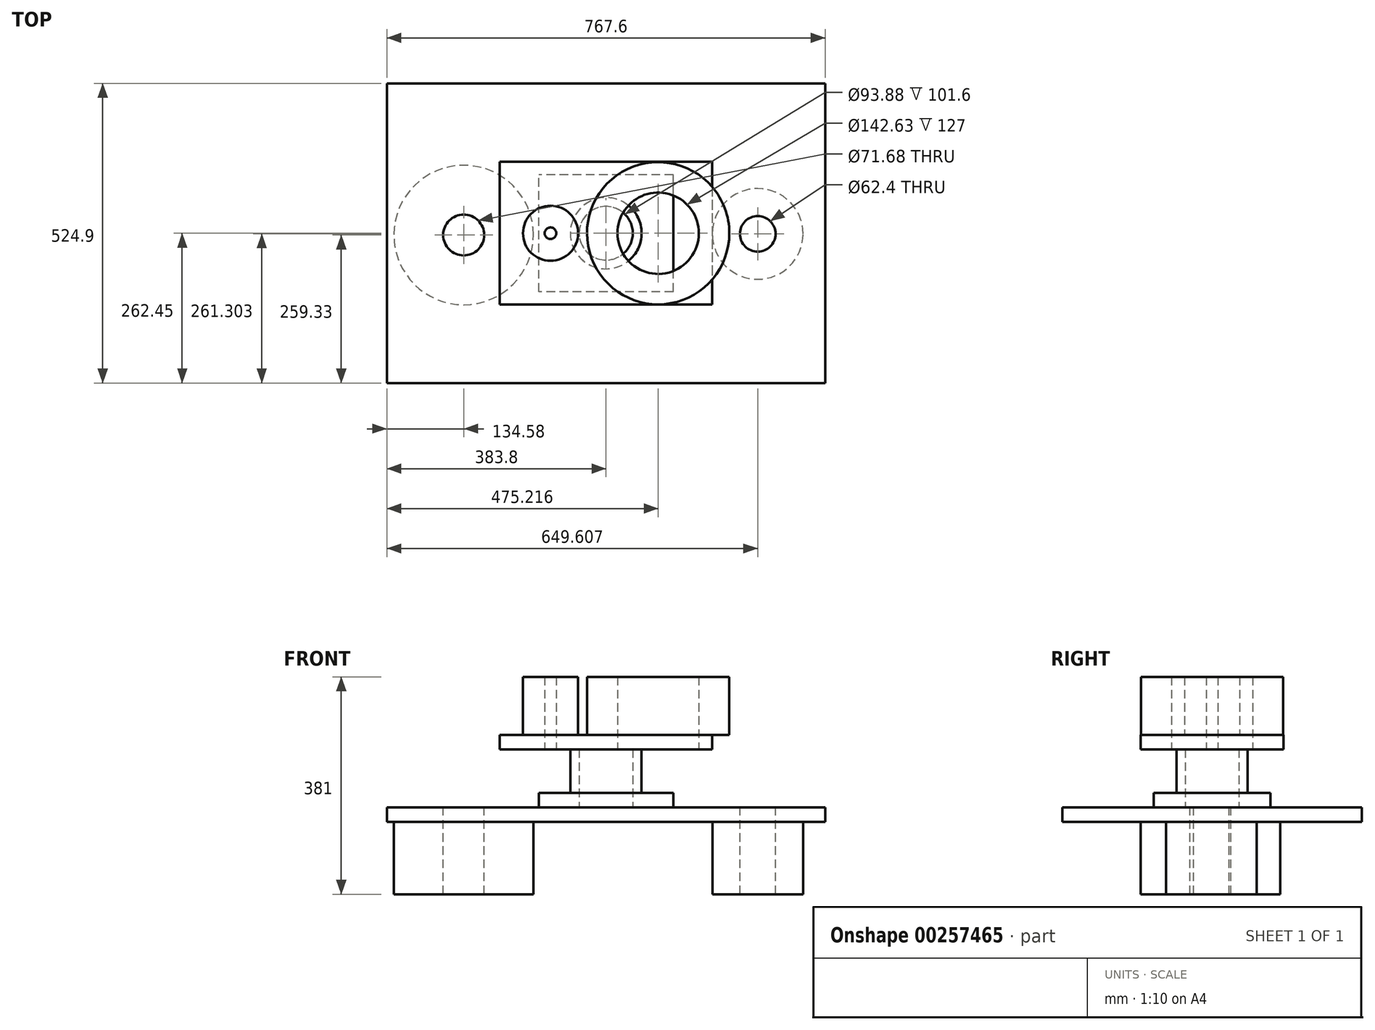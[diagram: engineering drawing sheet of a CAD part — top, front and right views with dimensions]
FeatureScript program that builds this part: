
annotation { "Feature Type Name" : "Feature", "Feature Type Description" : "" }
export const myFeature = defineFeature(function(context is Context, id is Id, definition is map)
    precondition{}
    {
        {
            var Q0;
            Q0=qCreatedBy(makeId("Top.planeOp"),FACE);
            var sketch = newSketch(context, id + "F0", { "sketchPlane" : qUnion([Q0])});
            skLineSegment(sketch, "E0.bottom", {"start": v(117.79, -102.4) * mm, "end": v(-117.79, -102.4) * mm});
            skLineSegment(sketch, "E0.top", {"start": v(117.79, 102.4) * mm, "end": v(-117.79, 102.4) * mm});
            skLineSegment(sketch, "E0.left", {"start": v(117.79, -102.4) * mm, "end": v(117.79, 102.4) * mm});
            skLineSegment(sketch, "E0.right", {"start": v(-117.79, -102.4) * mm, "end": v(-117.79, 102.4) * mm});
            skPoint(sketch, "E0.middle", {"position": v(0, 0) * mm});
            skCircle(sketch, "E1", {"center": v(0, 0) * mm, "radius": 46.94 * mm});
            skSolve(sketch);
        }
        {
            var Q0;
            Q0 = qSketchRegion(id + "F0", true);
            extrude(context, id + "F1", {"entities" : qUnion([Q0]), "depth" : 25.4 * mm});
        }
        {
            var Q0;
            Q0=makeQuery(id+"F1.opExtrude","CAP_FACE",FACE,{"disambiguationData":[OSD([sQuery(id+"F0.wireOp",EDGE,"E0.bottom"),sQuery(id+"F0.wireOp",EDGE,"E0.top"),sQuery(id+"F0.wireOp",EDGE,"E0.left"),sQuery(id+"F0.wireOp",EDGE,"E0.right"),sQuery(id+"F0.wireOp",EDGE,"E1")])],"isStart":false});
            var sketch = newSketch(context, id + "F2", { "sketchPlane" : qUnion([Q0])});
            skCircle(sketch, "E2.0", {"center": v(0, 0) * mm, "radius": 46.94 * mm});
            skCircle(sketch, "E3.0", {"center": v(0, 0) * mm, "radius": 62.43 * mm});
            skSolve(sketch);
        }
        {
            var Q0;
            Q0 = qSketchRegion(id + "F2", true);
            extrude(context, id + "F3", {"entities" : qUnion([Q0]), "operationType" : NewBodyOperationType.ADD, "depth" : 76.2 * mm});
        }
        {
            var Q0;
            Q0=makeQuery(id+"F3.opExtrude","CAP_FACE",FACE,{"disambiguationData":[OSD([sQuery(id+"F2.wireOp",EDGE,"E2.0"),sQuery(id+"F2.wireOp",EDGE,"E3.0")])],"isStart":false});
            var sketch = newSketch(context, id + "F4", { "sketchPlane" : qUnion([Q0])});
            skCircle(sketch, "E4", {"center": v(-97.13, 0) * mm, "radius": 10.19 * mm});
            skCircle(sketch, "E5", {"center": v(91.42, 0) * mm, "radius": 71.32 * mm});
            skLineSegment(sketch, "E6.bottom", {"start": v(185.83, 125.12) * mm, "end": v(-185.83, 125.12) * mm});
            skLineSegment(sketch, "E6.top", {"start": v(185.83, -125.12) * mm, "end": v(-185.83, -125.12) * mm});
            skLineSegment(sketch, "E6.left", {"start": v(185.83, 125.12) * mm, "end": v(185.83, -125.12) * mm});
            skLineSegment(sketch, "E6.right", {"start": v(-185.83, 125.12) * mm, "end": v(-185.83, -125.12) * mm});
            skPoint(sketch, "E6.middle", {"position": v(0, 0) * mm});
            skSolve(sketch);
        }
        {
            var Q0;
            Q0 = qSketchRegion(id + "F4", true);
            extrude(context, id + "F5", {"entities" : qUnion([Q0]), "operationType" : NewBodyOperationType.ADD, "depth" : 25.4 * mm});
        }
        {
            var Q0;
            Q0=makeQuery(id+"F5.opExtrude","CAP_FACE",FACE,{"disambiguationData":[OSD([sQuery(id+"F4.wireOp",EDGE,"E4"),sQuery(id+"F4.wireOp",EDGE,"E5"),sQuery(id+"F4.wireOp",EDGE,"E6.bottom"),sQuery(id+"F4.wireOp",EDGE,"E6.top"),sQuery(id+"F4.wireOp",EDGE,"E6.left"),sQuery(id+"F4.wireOp",EDGE,"E6.right")])],"isStart":false});
            var sketch = newSketch(context, id + "F6", { "sketchPlane" : qUnion([Q0])});
            skCircle(sketch, "E7.0", {"center": v(-97.13, 0) * mm, "radius": 10.19 * mm});
            skCircle(sketch, "E8.0", {"center": v(91.42, 0) * mm, "radius": 71.32 * mm});
            skCircle(sketch, "E9.0", {"center": v(-97.13, 0) * mm, "radius": 48.29 * mm});
            skCircle(sketch, "E10.0", {"center": v(91.42, 0) * mm, "radius": 124.66 * mm});
            skSolve(sketch);
        }
        {
            var Q0;
            Q0 = qSketchRegion(id + "F6", true);
            extrude(context, id + "F7", {"entities" : qUnion([Q0]), "operationType" : NewBodyOperationType.ADD, "depth" : 101.6 * mm});
        }
        {
            var Q0;
            Q0=makeQuery(id+"F1.opExtrude","CAP_FACE",FACE,{"disambiguationData":[OSD([sQuery(id+"F0.wireOp",EDGE,"E0.bottom"),sQuery(id+"F0.wireOp",EDGE,"E0.top"),sQuery(id+"F0.wireOp",EDGE,"E0.left"),sQuery(id+"F0.wireOp",EDGE,"E0.right"),sQuery(id+"F0.wireOp",EDGE,"E1")])],"isStart":true});
            var sketch = newSketch(context, id + "F8", { "sketchPlane" : qUnion([Q0])});
            skLineSegment(sketch, "E11.bottom", {"start": v(-383.8, 262.45) * mm, "end": v(383.8, 262.45) * mm});
            skLineSegment(sketch, "E11.top", {"start": v(-383.8, -262.45) * mm, "end": v(383.8, -262.45) * mm});
            skLineSegment(sketch, "E11.left", {"start": v(-383.8, 262.45) * mm, "end": v(-383.8, -262.45) * mm});
            skLineSegment(sketch, "E11.right", {"start": v(383.8, 262.45) * mm, "end": v(383.8, -262.45) * mm});
            skPoint(sketch, "E11.middle", {"position": v(0, 0) * mm});
            skCircle(sketch, "E12", {"center": v(265.8, 1.15) * mm, "radius": 31.2 * mm});
            skCircle(sketch, "E13", {"center": v(-249.22, 3.12) * mm, "radius": 35.84 * mm});
            skSolve(sketch);
        }
        {
            var Q0;
            Q0 = qSketchRegion(id + "F8", true);
            extrude(context, id + "F9", {"entities" : qUnion([Q0]), "operationType" : NewBodyOperationType.ADD, "depth" : 25.4 * mm});
        }
        {
            var Q0;
            Q0=makeQuery(id+"F9.opExtrude","CAP_FACE",FACE,{"disambiguationData":[OSD([sQuery(id+"F8.wireOp",EDGE,"E11.bottom"),sQuery(id+"F8.wireOp",EDGE,"E11.top"),sQuery(id+"F8.wireOp",EDGE,"E11.left"),sQuery(id+"F8.wireOp",EDGE,"E11.right"),sQuery(id+"F8.wireOp",EDGE,"E12"),sQuery(id+"F8.wireOp",EDGE,"E13")])],"isStart":false});
            var sketch = newSketch(context, id + "F10", { "sketchPlane" : qUnion([Q0])});
            skCircle(sketch, "E14.0", {"center": v(265.8, 1.15) * mm, "radius": 31.2 * mm});
            skCircle(sketch, "E15.0", {"center": v(-249.22, 3.12) * mm, "radius": 35.84 * mm});
            skCircle(sketch, "E16.0", {"center": v(265.8, 1.15) * mm, "radius": 79.46 * mm});
            skCircle(sketch, "E17.0", {"center": v(-249.22, 3.12) * mm, "radius": 122.2 * mm});
            skSolve(sketch);
        }
        {
            var Q0;
            Q0 = qSketchRegion(id + "F10", true);
            extrude(context, id + "F11", {"entities" : qUnion([Q0]), "operationType" : NewBodyOperationType.ADD, "depth" : 127 * mm});
        }
    });
